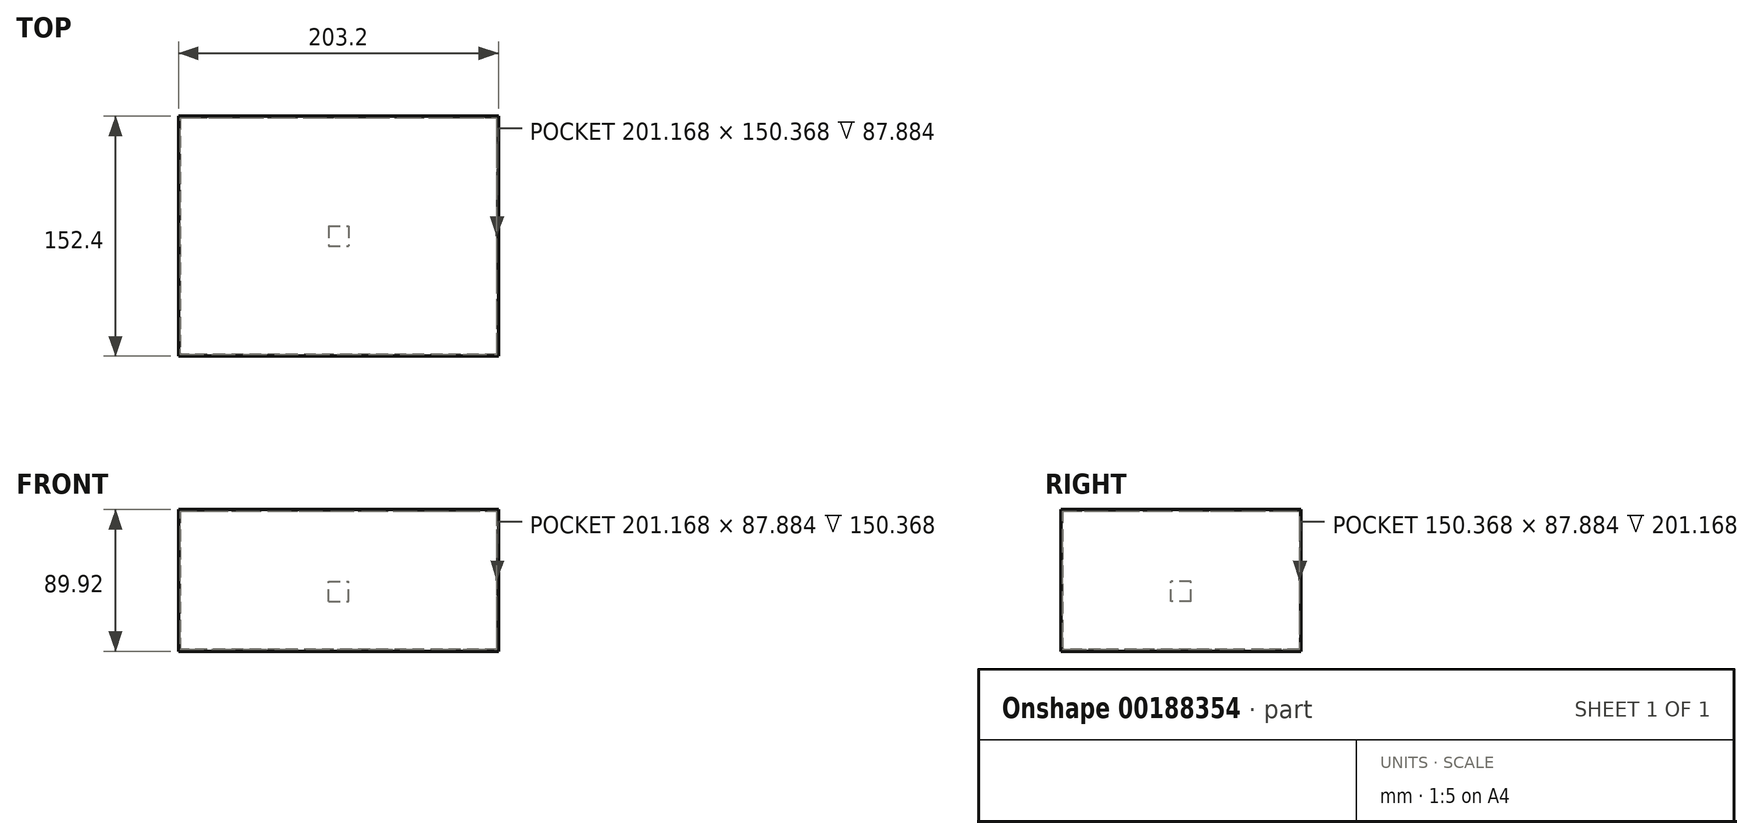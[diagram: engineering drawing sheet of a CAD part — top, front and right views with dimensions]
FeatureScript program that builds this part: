
annotation { "Feature Type Name" : "Feature", "Feature Type Description" : "" }
export const myFeature = defineFeature(function(context is Context, id is Id, definition is map)
    precondition{}
    {
        {
            var Q0;
            Q0=qCreatedBy(makeId("Top.planeOp"),FACE);
            var sketch = newSketch(context, id + "F0", { "sketchPlane" : qUnion([Q0])});
            skLineSegment(sketch, "E0.bottom", {"start": v(101.6, 76.2) * mm, "end": v(-101.6, 76.2) * mm});
            skLineSegment(sketch, "E0.top", {"start": v(101.6, -76.2) * mm, "end": v(-101.6, -76.2) * mm});
            skLineSegment(sketch, "E0.left", {"start": v(101.6, 76.2) * mm, "end": v(101.6, -76.2) * mm});
            skLineSegment(sketch, "E0.right", {"start": v(-101.6, 76.2) * mm, "end": v(-101.6, -76.2) * mm});
            skPoint(sketch, "E0.middle", {"position": v(0, 0) * mm});
            skSolve(sketch);
        }
        {
            var Q0;
            Q0=makeQuery(id+"F0.imprint","IMPRINT",FACE,{"disambiguationData":[TD([[makeQuery(id+"F0.imprint","IMPRINT",EDGE,{"derivedFrom":sQuery(id+"F0.wireOp",EDGE,"E0.bottom")}),1.0]])]});
            extrude(context, id + "F1", {"entities" : qUnion([Q0]), "depth" : 88.9 * mm});
        }
        {
            var Q0;
            Q0=makeQuery(id+"F1.opExtrude","CAP_FACE",FACE,{"disambiguationData":[OSD([sQuery(id+"F0.wireOp",EDGE,"E0.bottom"),sQuery(id+"F0.wireOp",EDGE,"E0.top"),sQuery(id+"F0.wireOp",EDGE,"E0.left"),sQuery(id+"F0.wireOp",EDGE,"E0.right")])],"isStart":false});
            shell(context, id + "F2", {"entities" : qUnion([Q0]), "thickness" : 1.02 * mm});
        }
        {
            var Q0;
            Q0=makeQuery(id+"F1.opExtrude","CAP_FACE",FACE,{"disambiguationData":[OSD([sQuery(id+"F0.wireOp",EDGE,"E0.bottom"),sQuery(id+"F0.wireOp",EDGE,"E0.top"),sQuery(id+"F0.wireOp",EDGE,"E0.left"),sQuery(id+"F0.wireOp",EDGE,"E0.right")])],"isStart":false});
            var sketch = newSketch(context, id + "F3", { "sketchPlane" : qUnion([Q0])});
            skLineSegment(sketch, "E1.bottom", {"start": v(-101.6, 76.2) * mm, "end": v(101.6, 76.2) * mm});
            skLineSegment(sketch, "E1.top", {"start": v(-101.6, -76.2) * mm, "end": v(101.6, -76.2) * mm});
            skLineSegment(sketch, "E1.left", {"start": v(-101.6, 76.2) * mm, "end": v(-101.6, -76.2) * mm});
            skLineSegment(sketch, "E1.right", {"start": v(101.6, 76.2) * mm, "end": v(101.6, -76.2) * mm});
            skSolve(sketch);
        }
        {
            var Q0;
            Q0 = qSketchRegion(id + "F3", true);
            extrude(context, id + "F4", {"entities" : qUnion([Q0]), "operationType" : NewBodyOperationType.ADD, "depth" : 1.02 * mm});
        }
        {
            var Q0;
            Q0=qCreatedBy(makeId("Right.planeOp"),FACE);
            cPlane(context, id + "F5", {"entities" : qUnion([Q0]), "cplaneType" : CPlaneType.OFFSET, "offset" : 6.35 * mm, "width" : 152.4 * mm, "height" : 152.4 * mm});
        }
        {
            var Q0;
            Q0=qCreatedBy(id+"F5.planeOp",FACE);
            var sketch = newSketch(context, id + "F6", { "sketchPlane" : qUnion([Q0])});
            skLineSegment(sketch, "E2.bottom", {"start": v(6.35, 31.75) * mm, "end": v(-6.35, 31.75) * mm});
            skLineSegment(sketch, "E2.top", {"start": v(6.35, 44.45) * mm, "end": v(-6.35, 44.45) * mm});
            skLineSegment(sketch, "E2.left", {"start": v(6.35, 31.75) * mm, "end": v(6.35, 44.45) * mm});
            skLineSegment(sketch, "E2.right", {"start": v(-6.35, 31.75) * mm, "end": v(-6.35, 44.45) * mm});
            skPoint(sketch, "E2.middle", {"position": v(0, 38.1) * mm});
            skSolve(sketch);
        }
        {
            var Q0;
            Q0=makeQuery(id+"F6.imprint","IMPRINT",FACE,{"disambiguationData":[TD([[makeQuery(id+"F6.imprint","IMPRINT",EDGE,{"derivedFrom":sQuery(id+"F6.wireOp",EDGE,"E2.bottom")}),-1.0]])]});
            extrude(context, id + "F7", {"entities" : qUnion([Q0]), "oppositeDirection" : true, "depth" : 12.7 * mm});
        }
    });
